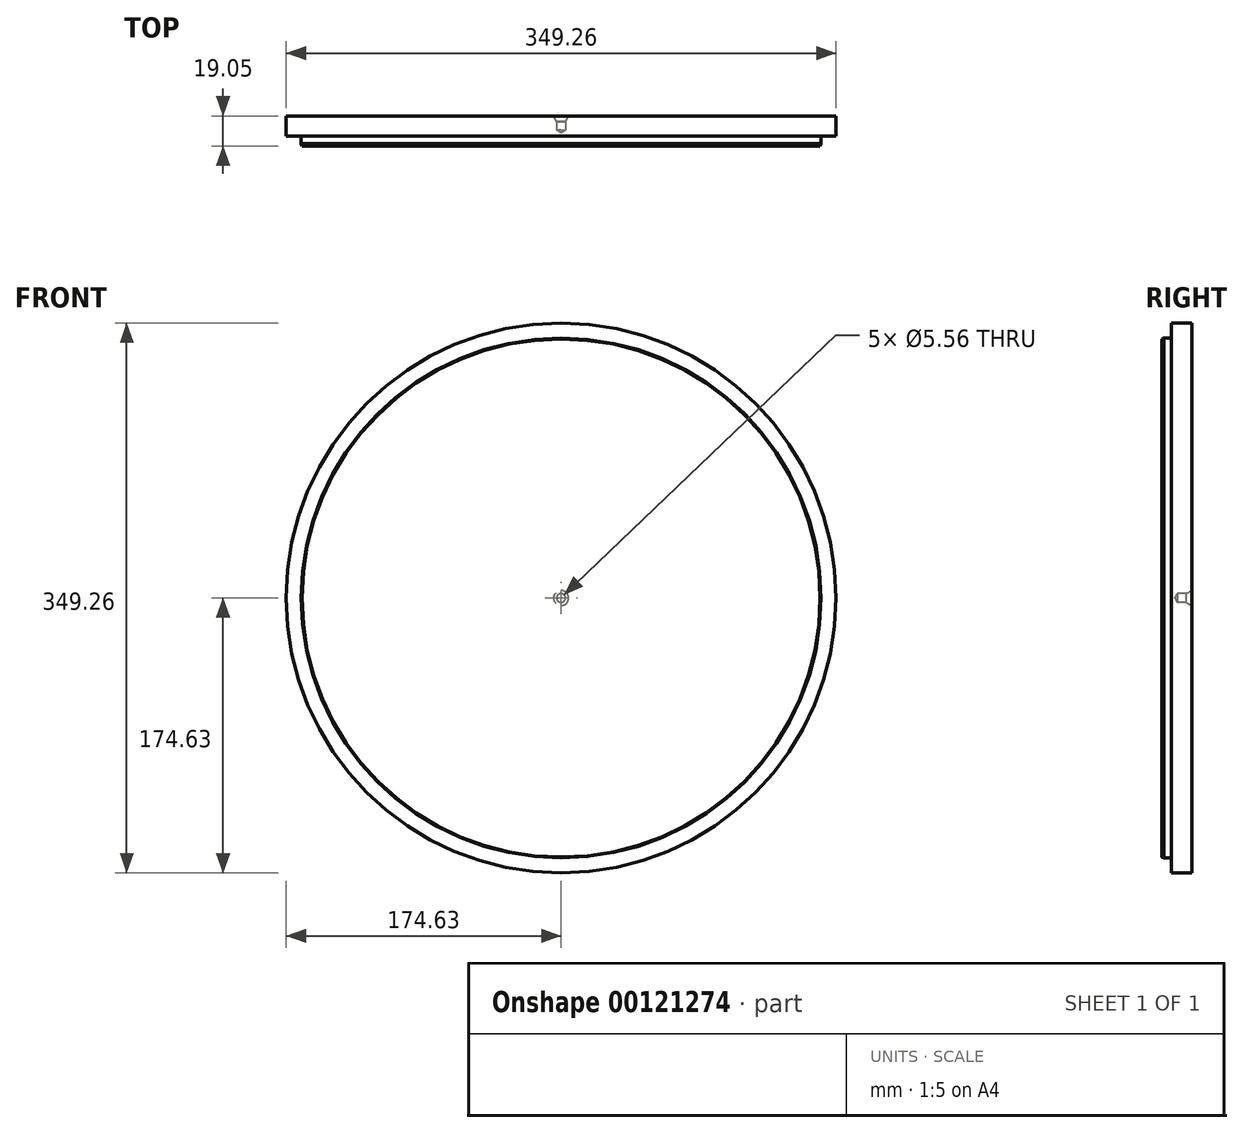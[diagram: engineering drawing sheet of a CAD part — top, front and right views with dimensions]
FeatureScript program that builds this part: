
annotation { "Feature Type Name" : "Feature", "Feature Type Description" : "" }
export const myFeature = defineFeature(function(context is Context, id is Id, definition is map)
    precondition{}
    {
        {
            var Q0;
            Q0=qCreatedBy(makeId("Right.planeOp"),FACE);
            var sketch = newSketch(context, id + "F0", { "sketchPlane" : qUnion([Q0])});
            skLineSegment(sketch, "E0", {"start": v(0, 4.77) * mm, "end": v(0, 174.62) * mm});
            skLineSegment(sketch, "E1", {"start": v(0, 174.62) * mm, "end": v(-12.7, 174.62) * mm});
            skLineSegment(sketch, "E2", {"start": v(-12.7, 174.62) * mm, "end": v(-12.7, 165.09) * mm});
            skLineSegment(sketch, "E3", {"start": v(-19.05, 0) * mm, "end": v(0, 0) * mm});
            skLineSegment(sketch, "E4", {"start": v(-17.53, 165.09) * mm, "end": v(-19.05, 164.53) * mm});
            skLineSegment(sketch, "E5", {"start": v(-12.7, 165.09) * mm, "end": v(-17.53, 165.09) * mm});
            skLineSegment(sketch, "E6", {"start": v(-17.53, 165.09) * mm, "end": v(-22.51, 165.09) * mm, "construction": true});
            skLineSegment(sketch, "E7", {"start": v(-19.05, 0) * mm, "end": v(-19.05, 164.53) * mm});
            skLineSegment(sketch, "E8", {"start": v(0, 4.77) * mm, "end": v(-3.45, 2.78) * mm});
            skLineSegment(sketch, "E9", {"start": v(-3.45, 2.78) * mm, "end": v(-9.01, 2.78) * mm});
            skLineSegment(sketch, "E10", {"start": v(-9.01, 2.78) * mm, "end": v(-10.68, 0) * mm});
            skSolve(sketch);
        }
        {
            var Q0;
            Q0 = qSketchRegion(id + "F0", true);
            var Q1;
            Q1=sQuery(id+"F0.wireOp",EDGE,"E3");
            revolve(context, id + "F1", {"entities" : qUnion([Q0]), "axis" : qUnion([Q1]), "revolveType" : RevolveType.FULL});
        }
    });
